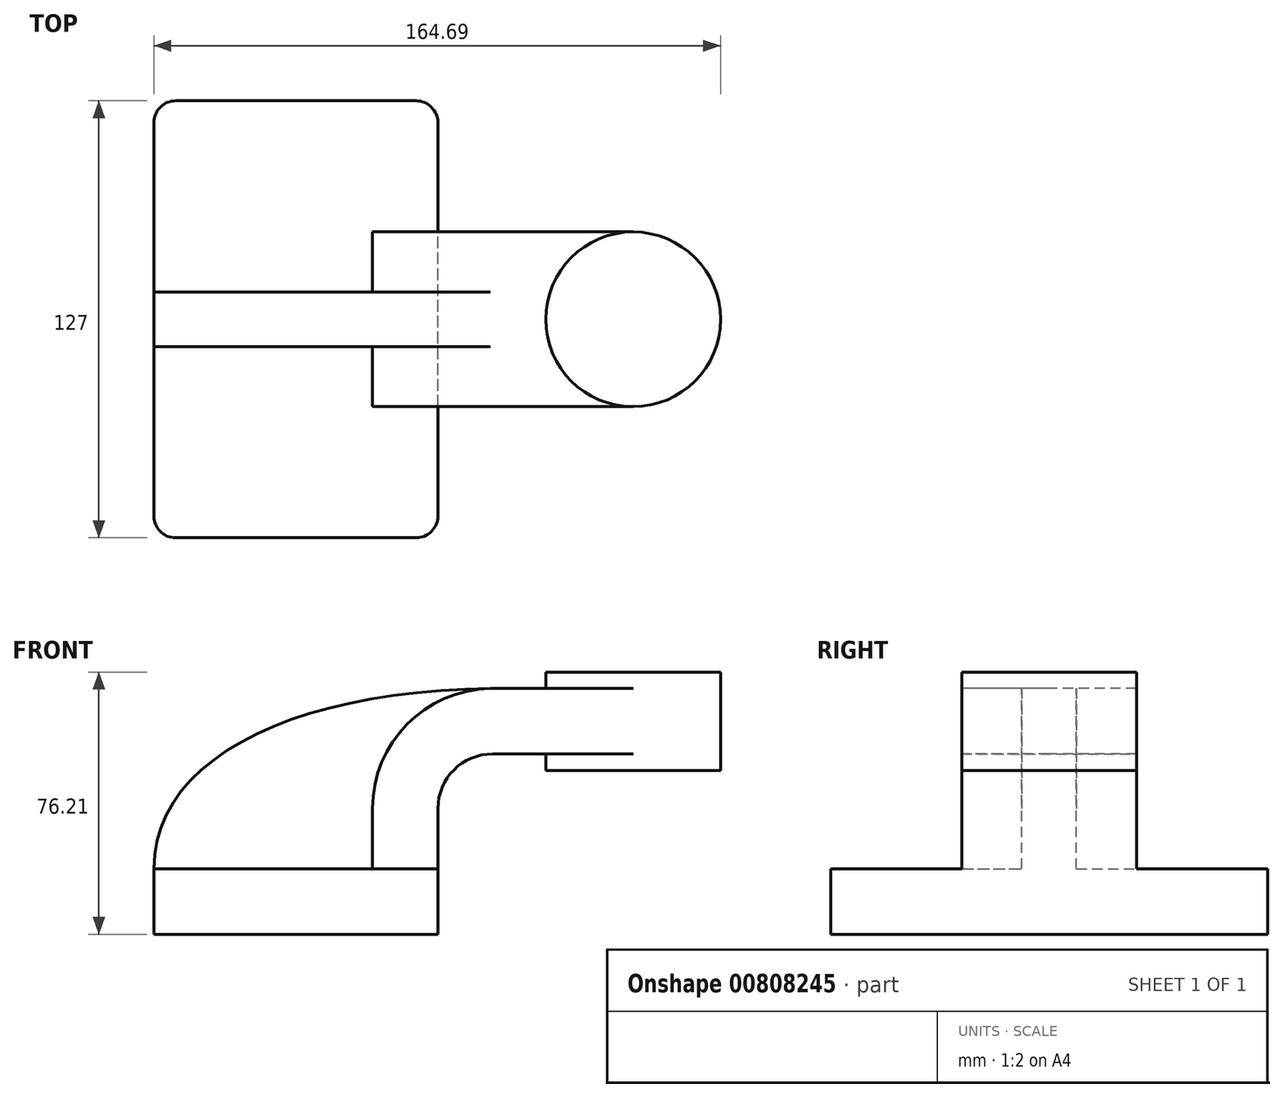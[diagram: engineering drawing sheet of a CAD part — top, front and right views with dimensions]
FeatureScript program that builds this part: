
annotation { "Feature Type Name" : "Feature", "Feature Type Description" : "" }
export const myFeature = defineFeature(function(context is Context, id is Id, definition is map)
    precondition{}
    {
        {
            var Q0;
            Q0=qCreatedBy(makeId("Front.planeOp"),FACE);
            var sketch = newSketch(context, id + "F0", { "sketchPlane" : qUnion([Q0])});
            skLineSegment(sketch, "E0.bottom", {"start": v(-41.28, -9.52) * mm, "end": v(41.28, -9.52) * mm});
            skLineSegment(sketch, "E0.top", {"start": v(-41.28, 9.53) * mm, "end": v(41.28, 9.53) * mm});
            skLineSegment(sketch, "E0.left", {"start": v(-41.28, -9.52) * mm, "end": v(-41.28, 9.53) * mm});
            skLineSegment(sketch, "E0.right", {"start": v(41.28, -9.53) * mm, "end": v(41.28, 9.52) * mm});
            skPoint(sketch, "E0.middle", {"position": v(0, 0) * mm});
            skLineSegment(sketch, "E1.bottom", {"start": v(72.61, 38.1) * mm, "end": v(123.41, 38.1) * mm});
            skLineSegment(sketch, "E1.top", {"start": v(72.61, 66.67) * mm, "end": v(123.41, 66.67) * mm});
            skLineSegment(sketch, "E1.left", {"start": v(72.61, 38.1) * mm, "end": v(72.61, 66.67) * mm});
            skLineSegment(sketch, "E1.right", {"start": v(123.41, 38.1) * mm, "end": v(123.41, 66.67) * mm});
            skPoint(sketch, "E1.middle", {"position": v(98.01, 52.39) * mm});
            skLineSegment(sketch, "E2", {"start": v(41.27, 9.52) * mm, "end": v(41.27, 27) * mm});
            skArc(sketch, "E3", {"start": v(41.27, 27) * mm, "mid": v(45.92, 38.23) * mm, "end": v(57.15, 42.88) * mm});
            skLineSegment(sketch, "E4", {"start": v(57.15, 42.88) * mm, "end": v(98.01, 42.88) * mm});
            skLineSegment(sketch, "E5.0", {"start": v(57.15, 61.87) * mm, "end": v(98.01, 61.87) * mm});
            skArc(sketch, "E5.1", {"start": v(22.28, 27) * mm, "mid": v(32.5, 51.66) * mm, "end": v(57.15, 61.87) * mm});
            skLineSegment(sketch, "E5.2", {"start": v(22.28, 9.52) * mm, "end": v(22.28, 27) * mm});
            skFitSpline(sketch, "E6", {"points": [v(-41.28, 9.53) * mm, v(57.15, 61.87) * mm], "startDerivative": vector(0.2, 96.74) * mm, "endDerivative": vector(171.45, 1.18) * mm});
            skLineSegment(sketch, "E7", {"start": v(98.01, 66.67) * mm, "end": v(98.01, 42.88) * mm});
            skLineSegment(sketch, "E8", {"start": v(98.01, 38.1) * mm, "end": v(98.01, 42.88) * mm});
            skSolve(sketch);
        }
        {
            var Q0;
            Q0=makeQuery(id+"F0.imprint","IMPRINT",FACE,{"disambiguationData":[TD([[makeQuery(id+"F0.imprint","IMPRINT",EDGE,{"derivedFrom":sQuery(id+"F0.wireOp",EDGE,"E0.bottom")}),1.0]])]});
            extrude(context, id + "F1", {"entities" : qUnion([Q0]), "depth" : 127 * mm, "offsetDistance" : 25.4 * mm, "symmetric" : true});
        }
        {
            var Q0;
            {var subQ1=sQuery(id+"F0.wireOp",EDGE,"E2");Q0=makeQuery(id+"F0.imprint","IMPRINT",FACE,{"disambiguationData":[TD([[makeQuery(id+"F0.imprint","IMPRINT",EDGE,{"derivedFrom":subQ1}),1.0]])]});}
            var Q1;
            {var subQ0=sQuery(id+"F0.wireOp",EDGE,"E4");var subQ1=sQuery(id+"F0.wireOp",EDGE,"E1.left");var subQ2=makeQuery(id+"F0.imprint","INTERSECT",VERTEX,{"derivedFrom":[subQ1,subQ0]});Q1=makeQuery(id+"F0.imprint","IMPRINT",FACE,{"disambiguationData":[TD([[makeQuery(id+"F0.imprint","IMPRINT",EDGE,{"disambiguationData":[TD([[subQ2,-1.0]])],"derivedFrom":subQ1}),-1.0]])]});}
            extrude(context, id + "F2", {"entities" : qUnion([Q0, Q1]), "operationType" : NewBodyOperationType.ADD, "depth" : 50.8 * mm, "offsetDistance" : 25.4 * mm, "symmetric" : true});
        }
        {
            var Q0;
            {var subQ3=sQuery(id+"F0.wireOp",EDGE,"E5.2");Q0=makeQuery(id+"F0.imprint","IMPRINT",FACE,{"disambiguationData":[TD([[makeQuery(id+"F0.imprint","IMPRINT",EDGE,{"derivedFrom":subQ3}),1.0]])]});}
            extrude(context, id + "F3", {"entities" : qUnion([Q0]), "operationType" : NewBodyOperationType.ADD, "depth" : 15.88 * mm, "offsetDistance" : 25.4 * mm, "symmetric" : true});
        }
        {
            var Q0;
            {var subQ4=sQuery(id+"F0.wireOp",EDGE,"E1.right");Q0=makeQuery(id+"F0.imprint","IMPRINT",FACE,{"disambiguationData":[TD([[makeQuery(id+"F0.imprint","IMPRINT",EDGE,{"derivedFrom":subQ4}),1.0]])]});}
            var Q1;
            Q1=sQuery(id+"F0.wireOp",EDGE,"E8");
            revolve(context, id + "F4", {"operationType" : NewBodyOperationType.ADD, "surfaceOperationType" : NewSurfaceOperationType.NEW, "entities" : qUnion([Q0]), "axis" : qUnion([Q1]), "revolveType" : RevolveType.FULL});
        }
        {
            var Q0;
            Q0=makeQuery(id+"F1.opExtrude","CAP_EDGE",EDGE,{"disambiguationData":[OSD([sQuery(id+"F0.wireOp",EDGE,"E0.left")])],"isStart":false});
            var Q1;
            Q1=makeQuery(id+"F1.opExtrude","CAP_EDGE",EDGE,{"disambiguationData":[OSD([sQuery(id+"F0.wireOp",EDGE,"E0.right")])],"isStart":false});
            var Q2;
            Q2=makeQuery(id+"F1.opExtrude","CAP_EDGE",EDGE,{"disambiguationData":[OSD([sQuery(id+"F0.wireOp",EDGE,"E0.right")])],"isStart":true});
            var Q3;
            Q3=makeQuery(id+"F1.opExtrude","CAP_EDGE",EDGE,{"disambiguationData":[OSD([sQuery(id+"F0.wireOp",EDGE,"E0.left")])],"isStart":true});
            fillet(context, id + "F5", {"entities" : qUnion([Q0, Q1, Q2, Q3]), "radius" : 6.35 * mm, "tangentPropagation" : true, "allowEdgeOverflow" : false});
        }
    });
